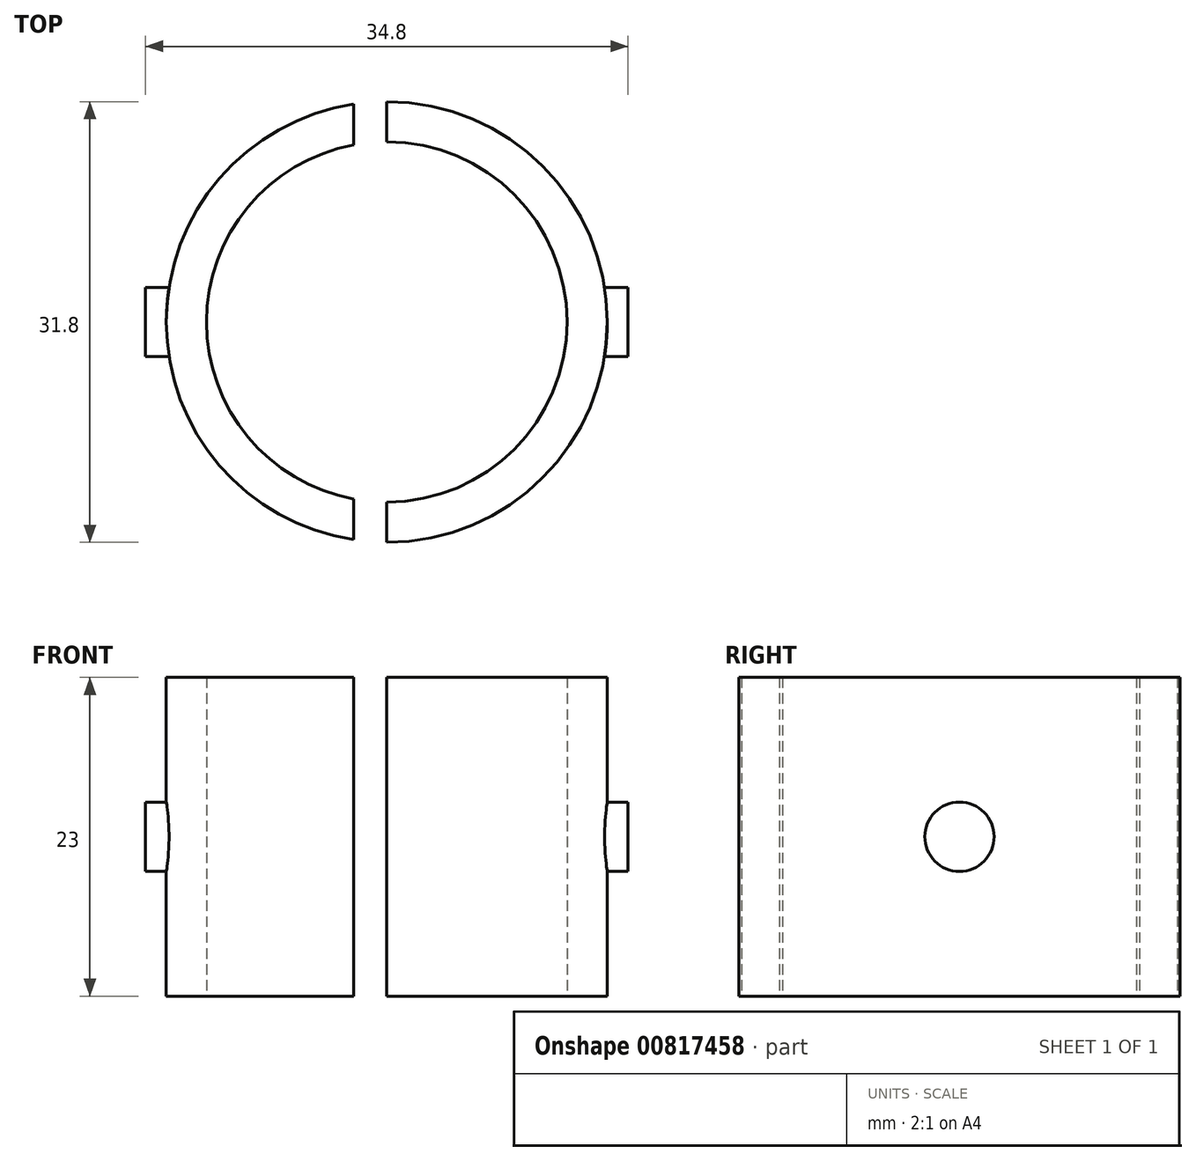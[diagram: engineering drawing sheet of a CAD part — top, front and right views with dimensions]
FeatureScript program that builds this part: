
annotation { "Feature Type Name" : "Feature", "Feature Type Description" : "" }
export const myFeature = defineFeature(function(context is Context, id is Id, definition is map)
    precondition{}
    {
        {
            var Q0;
            Q0=qCreatedBy(makeId("Top.planeOp"),FACE);
            var sketch = newSketch(context, id + "F0", { "sketchPlane" : qUnion([Q0])});
            skArc(sketch, "E0", {"start": v(-2.4, 12.78) * mm, "mid": v(-13, 0) * mm, "end": v(-2.4, -12.78) * mm});
            skArc(sketch, "E1.trimOffspring", {"start": v(0, -13) * mm, "mid": v(13, 0) * mm, "end": v(0, 13) * mm});
            skArc(sketch, "E2", {"start": v(-2.4, 15.72) * mm, "mid": v(-15.9, 0) * mm, "end": v(-2.4, -15.72) * mm});
            skLineSegment(sketch, "E3", {"start": v(-2.4, 15.72) * mm, "end": v(-2.4, 12.78) * mm});
            skArc(sketch, "E4.trimOffspring", {"start": v(0, -15.9) * mm, "mid": v(15.9, 0) * mm, "end": v(0, 15.9) * mm});
            skLineSegment(sketch, "E5.trimOffspring", {"start": v(-2.4, -12.78) * mm, "end": v(-2.4, -15.72) * mm});
            skLineSegment(sketch, "E6.trimOffspring", {"start": v(0, -13) * mm, "end": v(0, -15.9) * mm});
            skLineSegment(sketch, "E7", {"start": v(0, 15.9) * mm, "end": v(0, 13) * mm});
            skSolve(sketch);
        }
        {
            var Q0;
            Q0=makeQuery(id+"F0.imprint","IMPRINT",FACE,{"disambiguationData":[TD([[makeQuery(id+"F0.imprint","IMPRINT",EDGE,{"derivedFrom":sQuery(id+"F0.wireOp",EDGE,"E0")}),-1.0]])]});
            extrude(context, id + "F1", {"entities" : qUnion([Q0]), "depth" : 11.5 * mm, "offsetDistance" : 25 * mm, "hasSecondDirection" : true, "secondDirectionOppositeDirection" : true, "secondDirectionDepth" : 11.5 * mm});
        }
        {
            var Q0;
            Q0=makeQuery(id+"F0.imprint","IMPRINT",FACE,{"disambiguationData":[TD([[makeQuery(id+"F0.imprint","IMPRINT",EDGE,{"derivedFrom":sQuery(id+"F0.wireOp",EDGE,"E1.trimOffspring")}),-1.0]])]});
            extrude(context, id + "F2", {"entities" : qUnion([Q0]), "depth" : 11.5 * mm, "offsetDistance" : 25 * mm, "hasSecondDirection" : true, "secondDirectionOppositeDirection" : true, "secondDirectionDepth" : 11.5 * mm});
        }
        {
            var Q0;
            Q0=qCreatedBy(makeId("Right.planeOp"),FACE);
            var sketch = newSketch(context, id + "F3", { "sketchPlane" : qUnion([Q0])});
            skCircle(sketch, "E8", {"center": v(0, 0) * mm, "radius": 2.5 * mm});
            skSolve(sketch);
        }
        {
            var Q0;
            Q0=makeQuery(id+"F3.imprint","IMPRINT",FACE,{"disambiguationData":[TD([[makeQuery(id+"F3.imprint","IMPRINT",EDGE,{"derivedFrom":sQuery(id+"F3.wireOp",EDGE,"E8")}),1.0]])]});
            extrude(context, id + "F4", {"entities" : qUnion([Q0]), "operationType" : NewBodyOperationType.ADD, "depth" : 17.4 * mm, "offsetDistance" : 25 * mm, "hasSecondDirection" : true, "secondDirectionOppositeDirection" : false, "secondDirectionDepth" : 15 * mm});
        }
        {
            var Q0;
            Q0=makeQuery(id+"F3.imprint","IMPRINT",FACE,{"disambiguationData":[TD([[makeQuery(id+"F3.imprint","IMPRINT",EDGE,{"derivedFrom":sQuery(id+"F3.wireOp",EDGE,"E8")}),1.0]])]});
            extrude(context, id + "F5", {"entities" : qUnion([Q0]), "operationType" : NewBodyOperationType.ADD, "oppositeDirection" : true, "depth" : 17.4 * mm, "offsetDistance" : 25 * mm, "hasSecondDirection" : true, "secondDirectionOppositeDirection" : true, "secondDirectionDepth" : 15 * mm});
        }
    });
